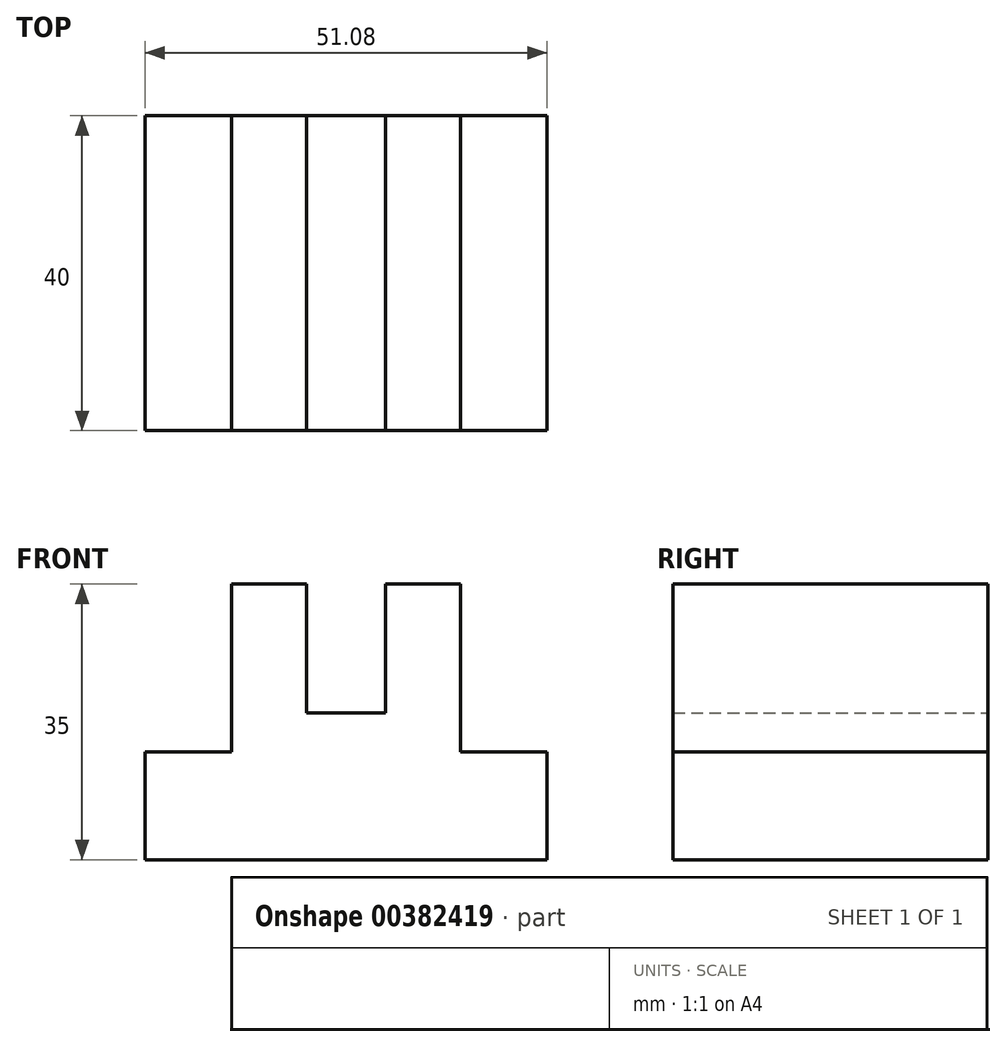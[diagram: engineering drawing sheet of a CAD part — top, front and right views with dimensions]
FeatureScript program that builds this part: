
annotation { "Feature Type Name" : "Feature", "Feature Type Description" : "" }
export const myFeature = defineFeature(function(context is Context, id is Id, definition is map)
    precondition{}
    {
        {
            var Q0;
            Q0=qCreatedBy(makeId("Front.planeOp"),FACE);
            var sketch = newSketch(context, id + "F0", { "sketchPlane" : qUnion([Q0])});
            skLineSegment(sketch, "E0.bottom", {"start": v(-26.37, -1.32) * mm, "end": v(24.71, -1.32) * mm});
            skLineSegment(sketch, "E0.top", {"start": v(-15.38, 33.68) * mm, "end": v(-5.83, 33.68) * mm});
            skLineSegment(sketch, "E0.left", {"start": v(-26.37, -1.32) * mm, "end": v(-26.37, 12.35) * mm});
            skLineSegment(sketch, "E0.right", {"start": v(24.71, -1.32) * mm, "end": v(24.71, 12.35) * mm});
            skLineSegment(sketch, "E1", {"start": v(13.71, 33.68) * mm, "end": v(13.71, 12.35) * mm});
            skLineSegment(sketch, "E2", {"start": v(13.71, 12.35) * mm, "end": v(24.71, 12.35) * mm});
            skLineSegment(sketch, "E3", {"start": v(-15.38, 33.68) * mm, "end": v(-15.38, 12.35) * mm});
            skLineSegment(sketch, "E4", {"start": v(-15.38, 12.35) * mm, "end": v(-26.37, 12.35) * mm});
            skLineSegment(sketch, "E5.trimOffspring", {"start": v(4.17, 33.68) * mm, "end": v(13.71, 33.68) * mm});
            skLineSegment(sketch, "E6", {"start": v(-5.83, 17.34) * mm, "end": v(4.17, 17.34) * mm});
            skLineSegment(sketch, "E7", {"start": v(4.17, 17.34) * mm, "end": v(4.17, 33.68) * mm});
            skLineSegment(sketch, "E8", {"start": v(-5.83, 17.34) * mm, "end": v(-5.83, 33.68) * mm});
            skSolve(sketch);
        }
        {
            var Q0;
            Q0 = qSketchRegion(id + "F0", true);
            extrude(context, id + "F1", {"entities" : qUnion([Q0]), "depth" : 40 * mm});
        }
    });
